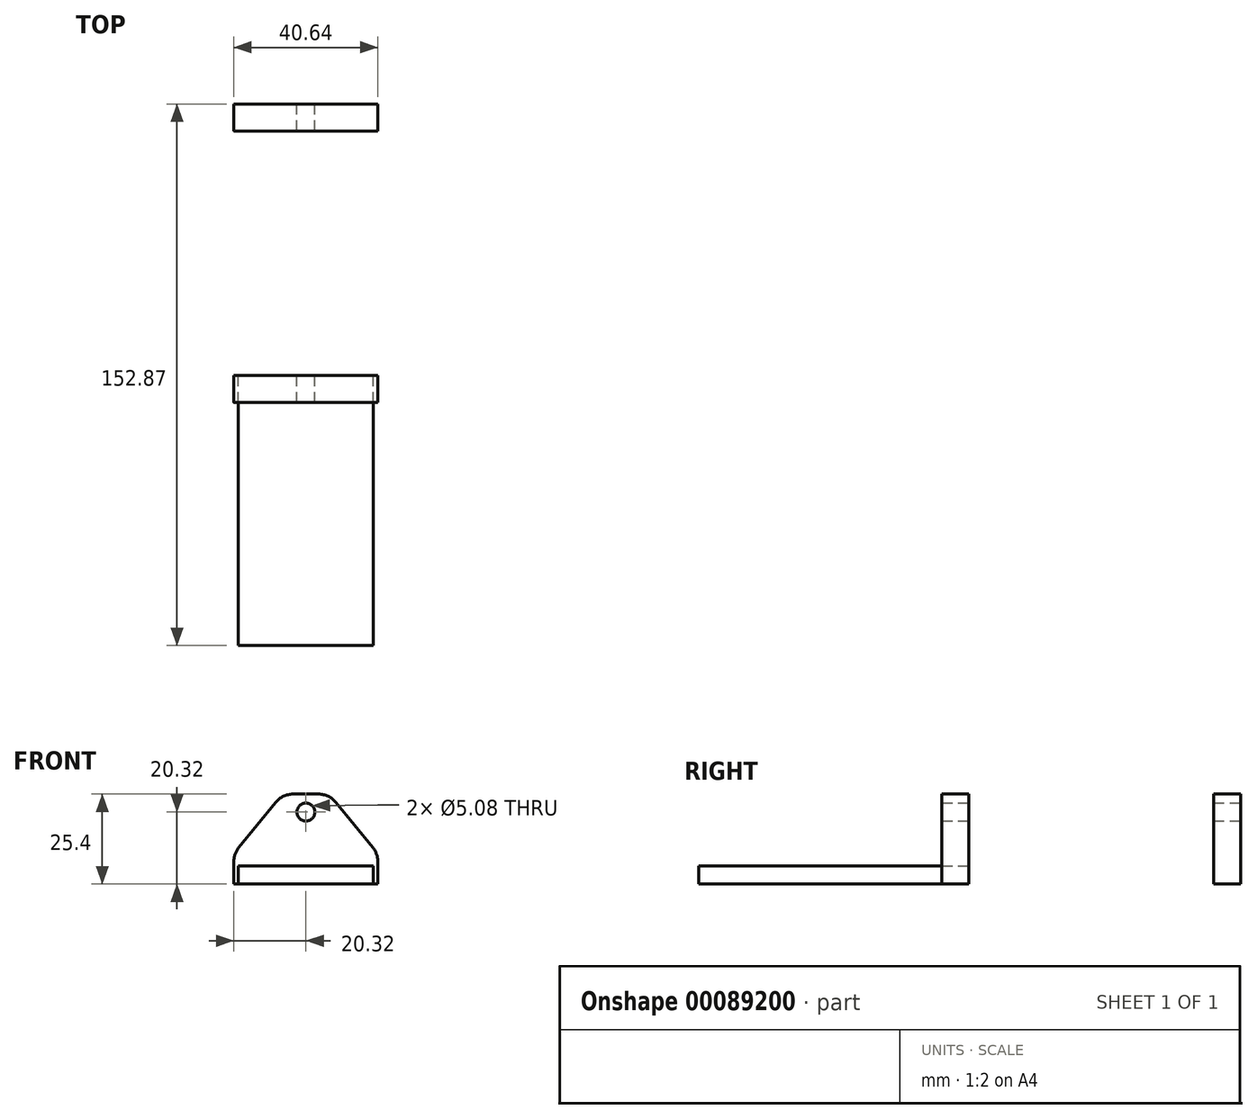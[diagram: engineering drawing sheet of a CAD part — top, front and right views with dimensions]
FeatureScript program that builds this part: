
annotation { "Feature Type Name" : "Feature", "Feature Type Description" : "" }
export const myFeature = defineFeature(function(context is Context, id is Id, definition is map)
    precondition{}
    {
        {
            var Q0;
            Q0=qCreatedBy(makeId("Front.planeOp"),FACE);
            var sketch = newSketch(context, id + "F0", { "sketchPlane" : qUnion([Q0])});
            skLineSegment(sketch, "E0", {"start": v(-20.32, 0) * mm, "end": v(-20.32, 6.35) * mm});
            skLineSegment(sketch, "E1", {"start": v(-18.89, 10.37) * mm, "end": v(-8.5, 23.07) * mm});
            skLineSegment(sketch, "E2", {"start": v(-3.6, 25.4) * mm, "end": v(3.6, 25.4) * mm});
            skLineSegment(sketch, "E3", {"start": v(8.5, 23.07) * mm, "end": v(18.89, 10.37) * mm});
            skLineSegment(sketch, "E4", {"start": v(20.32, 6.35) * mm, "end": v(20.32, 0) * mm});
            skLineSegment(sketch, "E5", {"start": v(-20.32, 0) * mm, "end": v(20.32, 0) * mm});
            skPoint(sketch, "E6.visualSharp", {"position": v(-20.32, 8.61) * mm});
            skArc(sketch, "E6.filletArc", {"start": v(-18.89, 10.37) * mm, "mid": v(-19.95, 8.48) * mm, "end": v(-20.32, 6.35) * mm});
            skPoint(sketch, "E7.visualSharp", {"position": v(-6.6, 25.4) * mm});
            skArc(sketch, "E7.filletArc", {"start": v(-3.6, 25.4) * mm, "mid": v(-6.31, 24.79) * mm, "end": v(-8.5, 23.07) * mm});
            skPoint(sketch, "E8.visualSharp", {"position": v(6.6, 25.4) * mm});
            skArc(sketch, "E8.filletArc", {"start": v(8.5, 23.07) * mm, "mid": v(6.31, 24.79) * mm, "end": v(3.6, 25.4) * mm});
            skPoint(sketch, "E9.visualSharp", {"position": v(20.32, 8.61) * mm});
            skArc(sketch, "E9.filletArc", {"start": v(20.32, 6.35) * mm, "mid": v(19.95, 8.48) * mm, "end": v(18.89, 10.37) * mm});
            skCircle(sketch, "E10", {"center": v(0, 20.32) * mm, "radius": 2.54 * mm});
            skSolve(sketch);
        }
        {
            var Q0;
            Q0=makeQuery(id+"F0.imprint","IMPRINT",FACE,{"disambiguationData":[TD([[makeQuery(id+"F0.imprint","IMPRINT",EDGE,{"derivedFrom":sQuery(id+"F0.wireOp",EDGE,"E0")}),-1.0]])]});
            extrude(context, id + "F1", {"entities" : qUnion([Q0]), "depth" : 7.62 * mm});
        }
        {
            var Q0;
            Q0=makeQuery(id+"F1.opExtrude","SWEPT_BODY",BODY,{"disambiguationData":[OSD([sQuery(id+"F0.wireOp",EDGE,"E0"),sQuery(id+"F0.wireOp",EDGE,"E1"),sQuery(id+"F0.wireOp",EDGE,"E2"),sQuery(id+"F0.wireOp",EDGE,"E3"),sQuery(id+"F0.wireOp",EDGE,"E4"),sQuery(id+"F0.wireOp",EDGE,"E5"),sQuery(id+"F0.wireOp",EDGE,"E6.filletArc"),sQuery(id+"F0.wireOp",EDGE,"E7.filletArc"),sQuery(id+"F0.wireOp",EDGE,"E8.filletArc"),sQuery(id+"F0.wireOp",EDGE,"E9.filletArc"),sQuery(id+"F0.wireOp",EDGE,"E10")])]});
            transform(context, id + "F2", {"entities" : qUnion([Q0]), "transformType" : TransformType.TRANSLATION_3D, "dx" : 0 * mm, "dy" : 76.67 * mm, "dz" : 0 * mm, "makeCopy" : true});
        }
        {
            var Q0;
            Q0=qCreatedBy(makeId("Front.planeOp"),FACE);
            var sketch = newSketch(context, id + "F3", { "sketchPlane" : qUnion([Q0])});
            skLineSegment(sketch, "E11.bottom", {"start": v(-19.05, 5.08) * mm, "end": v(19.05, 5.08) * mm});
            skLineSegment(sketch, "E11.top", {"start": v(-19.05, 0) * mm, "end": v(19.05, 0) * mm});
            skLineSegment(sketch, "E11.left", {"start": v(-19.05, 5.08) * mm, "end": v(-19.05, 0) * mm});
            skLineSegment(sketch, "E11.right", {"start": v(19.05, 5.08) * mm, "end": v(19.05, 0) * mm});
            skSolve(sketch);
        }
        {
            var Q0;
            Q0=makeQuery(id+"F3.imprint","IMPRINT",FACE,{"disambiguationData":[TD([[makeQuery(id+"F3.imprint","IMPRINT",EDGE,{"derivedFrom":sQuery(id+"F3.wireOp",EDGE,"E11.bottom")}),-1.0]])]});
            extrude(context, id + "F4", {"entities" : qUnion([Q0]), "depth" : 76.2 * mm});
        }
    });
